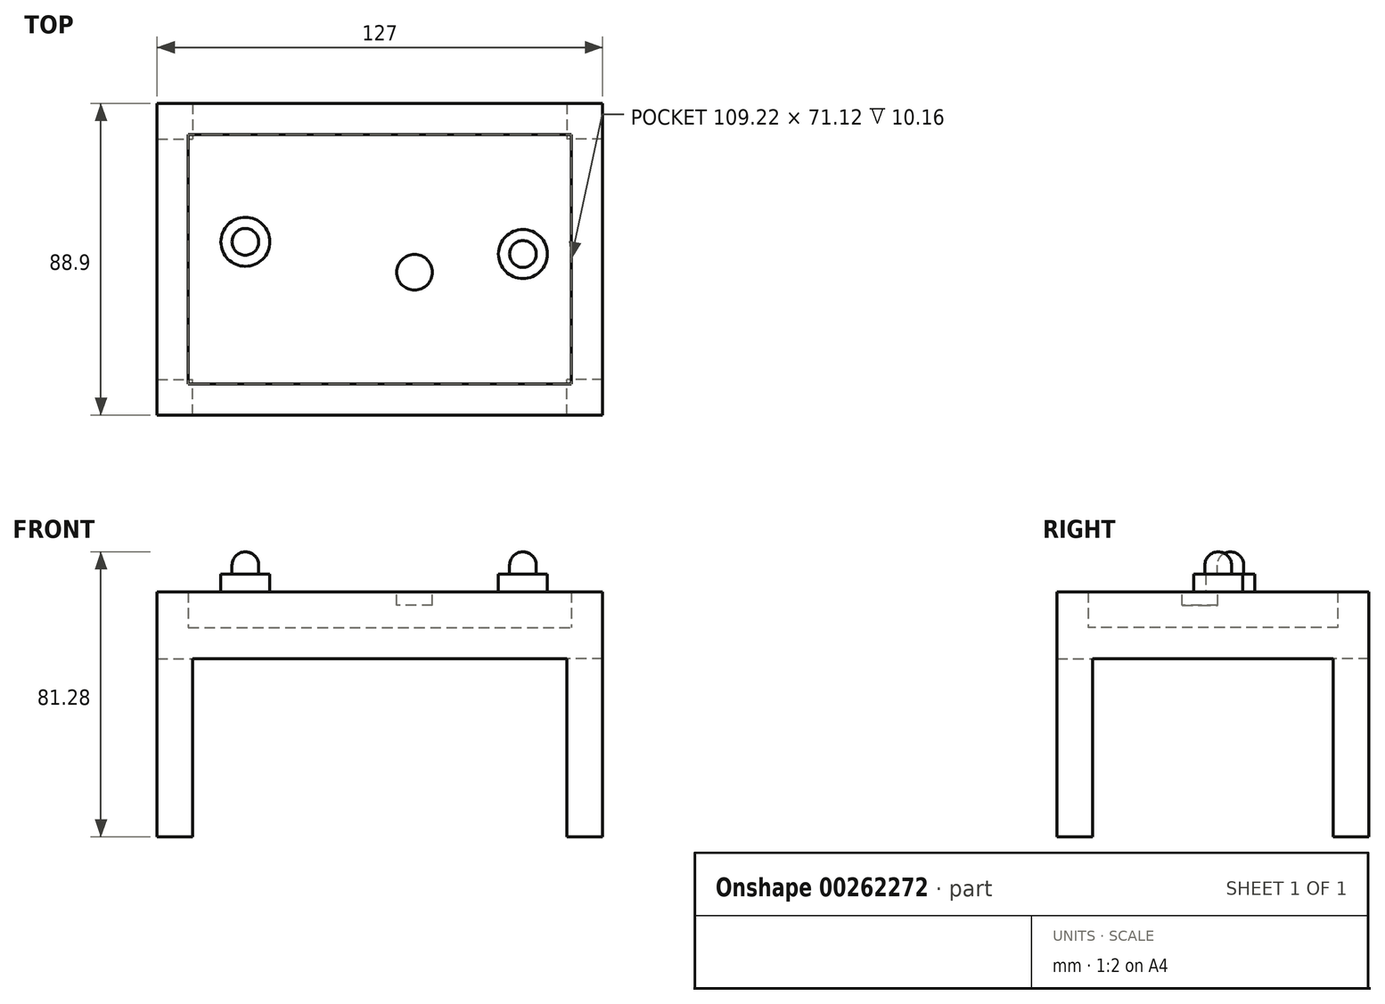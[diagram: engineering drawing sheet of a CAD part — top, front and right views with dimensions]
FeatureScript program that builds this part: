
annotation { "Feature Type Name" : "Feature", "Feature Type Description" : "" }
export const myFeature = defineFeature(function(context is Context, id is Id, definition is map)
    precondition{}
    {
        {
            var Q0;
            Q0=qCreatedBy(makeId("Top.planeOp"),FACE);
            var sketch = newSketch(context, id + "F0", { "sketchPlane" : qUnion([Q0])});
            skLineSegment(sketch, "E0.bottom", {"start": v(-63.5, 44.45) * mm, "end": v(63.5, 44.45) * mm});
            skLineSegment(sketch, "E0.top", {"start": v(-63.5, -44.45) * mm, "end": v(63.5, -44.45) * mm});
            skLineSegment(sketch, "E0.left", {"start": v(-63.5, 44.45) * mm, "end": v(-63.5, -44.45) * mm});
            skLineSegment(sketch, "E0.right", {"start": v(63.5, 44.45) * mm, "end": v(63.5, -44.45) * mm});
            skPoint(sketch, "E0.middle", {"position": v(0, 0) * mm});
            skSolve(sketch);
        }
        {
            var Q0;
            Q0=makeQuery(id+"F0.imprint","IMPRINT",FACE,{"disambiguationData":[TD([[makeQuery(id+"F0.imprint","IMPRINT",EDGE,{"derivedFrom":sQuery(id+"F0.wireOp",EDGE,"E0.bottom")}),-1.0]])]});
            extrude(context, id + "F1", {"entities" : qUnion([Q0]), "depth" : 19.05 * mm});
        }
        {
            var Q0;
            Q0=makeQuery(id+"F1.opExtrude","CAP_FACE",FACE,{"disambiguationData":[OSD([sQuery(id+"F0.wireOp",EDGE,"E0.bottom"),sQuery(id+"F0.wireOp",EDGE,"E0.top"),sQuery(id+"F0.wireOp",EDGE,"E0.left"),sQuery(id+"F0.wireOp",EDGE,"E0.right")])],"isStart":false});
            var sketch = newSketch(context, id + "F2", { "sketchPlane" : qUnion([Q0])});
            skLineSegment(sketch, "E1.bottom", {"start": v(-53.34, 35.56) * mm, "end": v(53.34, 35.56) * mm});
            skLineSegment(sketch, "E1.top", {"start": v(-53.34, -35.56) * mm, "end": v(53.34, -35.56) * mm});
            skLineSegment(sketch, "E1.left", {"start": v(-53.34, 35.56) * mm, "end": v(-53.34, -35.56) * mm});
            skLineSegment(sketch, "E1.right", {"start": v(53.34, 35.56) * mm, "end": v(53.34, -35.56) * mm});
            skPoint(sketch, "E1.middle", {"position": v(0, 0) * mm});
            skSolve(sketch);
        }
        {
            var Q0;
            Q0=makeQuery(id+"F1.opExtrude","CAP_FACE",FACE,{"disambiguationData":[OSD([sQuery(id+"F0.wireOp",EDGE,"E0.bottom"),sQuery(id+"F0.wireOp",EDGE,"E0.top"),sQuery(id+"F0.wireOp",EDGE,"E0.left"),sQuery(id+"F0.wireOp",EDGE,"E0.right")])],"isStart":false});
            shell(context, id + "F3", {"entities" : qUnion([Q0]), "thickness" : 8.9 * mm});
        }
        {
            var Q0;
            Q0=makeQuery(id+"F1.opExtrude","CAP_FACE",FACE,{"disambiguationData":[OSD([sQuery(id+"F0.wireOp",EDGE,"E0.bottom"),sQuery(id+"F0.wireOp",EDGE,"E0.top"),sQuery(id+"F0.wireOp",EDGE,"E0.left"),sQuery(id+"F0.wireOp",EDGE,"E0.right")])],"isStart":true});
            var sketch = newSketch(context, id + "F4", { "sketchPlane" : qUnion([Q0])});
            skLineSegment(sketch, "E2.bottom", {"start": v(-63.5, -44.45) * mm, "end": v(-53.34, -44.45) * mm});
            skLineSegment(sketch, "E2.top", {"start": v(-63.5, -34.3) * mm, "end": v(-53.34, -34.3) * mm});
            skLineSegment(sketch, "E2.left", {"start": v(-63.5, -44.45) * mm, "end": v(-63.5, -34.3) * mm});
            skLineSegment(sketch, "E2.right", {"start": v(-53.34, -44.45) * mm, "end": v(-53.34, -34.3) * mm});
            skLineSegment(sketch, "E3.bottom", {"start": v(63.5, -44.45) * mm, "end": v(53.34, -44.45) * mm});
            skLineSegment(sketch, "E3.top", {"start": v(63.5, -34.3) * mm, "end": v(53.34, -34.3) * mm});
            skLineSegment(sketch, "E3.left", {"start": v(63.5, -44.45) * mm, "end": v(63.5, -34.3) * mm});
            skLineSegment(sketch, "E3.right", {"start": v(53.34, -44.45) * mm, "end": v(53.34, -34.3) * mm});
            skLineSegment(sketch, "E4.bottom", {"start": v(-63.5, 44.45) * mm, "end": v(-53.34, 44.45) * mm});
            skLineSegment(sketch, "E4.top", {"start": v(-63.5, 34.3) * mm, "end": v(-53.34, 34.3) * mm});
            skLineSegment(sketch, "E4.left", {"start": v(-63.5, 44.45) * mm, "end": v(-63.5, 34.3) * mm});
            skLineSegment(sketch, "E4.right", {"start": v(-53.34, 44.45) * mm, "end": v(-53.34, 34.3) * mm});
            skLineSegment(sketch, "E5.bottom", {"start": v(63.5, 44.45) * mm, "end": v(53.34, 44.45) * mm});
            skLineSegment(sketch, "E5.top", {"start": v(63.5, 34.3) * mm, "end": v(53.34, 34.3) * mm});
            skLineSegment(sketch, "E5.left", {"start": v(63.5, 44.45) * mm, "end": v(63.5, 34.3) * mm});
            skLineSegment(sketch, "E5.right", {"start": v(53.34, 44.45) * mm, "end": v(53.34, 34.29) * mm});
            skSolve(sketch);
        }
        {
            var Q0;
            Q0 = qSketchRegion(id + "F4", true);
            extrude(context, id + "F5", {"entities" : qUnion([Q0]), "operationType" : NewBodyOperationType.ADD, "depth" : 50.8 * mm});
        }
        {
            var Q0;
            Q0=makeQuery(id+"F2.imprint","IMPRINT",FACE,{"disambiguationData":[TD([[makeQuery(id+"F2.imprint","IMPRINT",EDGE,{"derivedFrom":sQuery(id+"F2.wireOp",EDGE,"E1.bottom")}),-1.0]])]});
            var sketch = newSketch(context, id + "F6", { "sketchPlane" : qUnion([Q0])});
            skCircle(sketch, "E6", {"center": v(9.89, -3.72) * mm, "radius": 5.08 * mm});
            skSolve(sketch);
        }
        {
            var Q0;
            Q0 = qSketchRegion(id + "F6", true);
            extrude(context, id + "F7", {"entities" : qUnion([Q0]), "oppositeDirection" : true, "depth" : 3.8 * mm});
        }
        {
            var Q0;
            Q0=makeQuery(id+"F2.imprint","IMPRINT",FACE,{"disambiguationData":[TD([[makeQuery(id+"F2.imprint","IMPRINT",EDGE,{"derivedFrom":sQuery(id+"F2.wireOp",EDGE,"E1.bottom")}),-1.0]])]});
            var sketch = newSketch(context, id + "F8", { "sketchPlane" : qUnion([Q0])});
            skCircle(sketch, "E7", {"center": v(40.78, 1.5) * mm, "radius": 6.99 * mm});
            skSolve(sketch);
        }
        {
            var Q0;
            Q0 = qSketchRegion(id + "F8", true);
            extrude(context, id + "F9", {"entities" : qUnion([Q0]), "depth" : 5.08 * mm});
        }
        {
            var Q0;
            Q0=makeQuery(id+"F9.opExtrude","CAP_FACE",FACE,{"disambiguationData":[OSD([sQuery(id+"F8.wireOp",EDGE,"E7")])],"isStart":false});
            var sketch = newSketch(context, id + "F10", { "sketchPlane" : qUnion([Q0])});
            skCircle(sketch, "E8", {"center": v(40.78, 1.5) * mm, "radius": 3.81 * mm});
            skSolve(sketch);
        }
        {
            var Q0;
            Q0 = qSketchRegion(id + "F10", true);
            extrude(context, id + "F11", {"entities" : qUnion([Q0]), "operationType" : NewBodyOperationType.ADD, "depth" : 6.35 * mm});
        }
        {
            var Q0;
            Q0=makeQuery(id+"F11.opExtrude","CAP_EDGE",EDGE,{"disambiguationData":[OSD([sQuery(id+"F10.wireOp",EDGE,"E8")])],"isStart":false});
            fillet(context, id + "F12", {"entities" : qUnion([Q0]), "radius" : 3.8 * mm, "tangentPropagation" : true, "allowEdgeOverflow" : false});
        }
        {
            var Q0;
            Q0=makeQuery(id+"F2.imprint","IMPRINT",FACE,{"disambiguationData":[TD([[makeQuery(id+"F2.imprint","IMPRINT",EDGE,{"derivedFrom":sQuery(id+"F2.wireOp",EDGE,"E1.bottom")}),-1.0]])]});
            var sketch = newSketch(context, id + "F13", { "sketchPlane" : qUnion([Q0])});
            skCircle(sketch, "E9", {"center": v(-38.35, 4.98) * mm, "radius": 6.99 * mm});
            skSolve(sketch);
        }
        {
            var Q0;
            Q0 = qSketchRegion(id + "F13", true);
            extrude(context, id + "F14", {"entities" : qUnion([Q0]), "depth" : 5.08 * mm});
        }
        {
            var Q0;
            Q0=makeQuery(id+"F14.opExtrude","CAP_FACE",FACE,{"disambiguationData":[OSD([sQuery(id+"F13.wireOp",EDGE,"E9")])],"isStart":false});
            var sketch = newSketch(context, id + "F15", { "sketchPlane" : qUnion([Q0])});
            skCircle(sketch, "E10", {"center": v(-38.35, 4.98) * mm, "radius": 3.8 * mm});
            skSolve(sketch);
        }
        {
            var Q0;
            Q0 = qSketchRegion(id + "F15", true);
            extrude(context, id + "F16", {"entities" : qUnion([Q0]), "operationType" : NewBodyOperationType.ADD, "depth" : 6.35 * mm});
        }
        {
            var Q0;
            Q0=makeQuery(id+"F16.opExtrude","CAP_EDGE",EDGE,{"disambiguationData":[OSD([sQuery(id+"F15.wireOp",EDGE,"E10")])],"isStart":false});
            fillet(context, id + "F17", {"entities" : qUnion([Q0]), "radius" : 3.8 * mm, "tangentPropagation" : true, "allowEdgeOverflow" : false});
        }
    });
